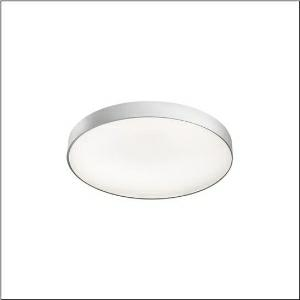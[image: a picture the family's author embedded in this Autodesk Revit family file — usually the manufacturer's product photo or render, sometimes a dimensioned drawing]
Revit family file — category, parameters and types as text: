
# Revit family: round_21_m_51mr36nd0421s
name_source: partatom
category: Lighting Fixtures
units: mm (PartAtom-declared; Revit-internal decimal feet)

## family parameters
Cut with Voids When Loaded = No
Host = Face
Light Source = No
Part Type = Normal
Room Calculation Point = No
Round Connector Dimension = Use Diameter
Shared = No

## types (1)
- Round 21 M (1 x LED, 7470 lm, 54.6 W, 4000K)
    Apparent Load = 55 VA
    CIE Flux Codes = 66 90 98 84 100
    Color Rendering = 80
    Color Temperature = 4000K
    Default Elevation = 1800 mm
    Description = Round 21 M, wall and ceiling luminaire, primary optical cover: micro prismatic cover, of PMMA, transparent, CAT 2 (L<= 3000cd/m²), light emission: direct/indirect distribution, primary light characteristic: symmetric, installation type: surface-mounted, suspended mounting, LED, rated luminous flux: 7.470lm, luminous efficacy: 137lm/W, light colour: 840, colour temperature: 4000K, control gear: DALI 2, with terminal, 5-pole, mains connection: 230V, AC, 50/60Hz, rated input power: 54.6W, housing, of aluminium, coated, silver, diameter: 600mm, height: 62mm, protection rating (complete): IP40, insulation class (complete): insulation class I (protective earthing), certification: CE, impact resistance: IK04, permissible operating ambient temperature: -10..+35°C, packaging unit: 1 piece
    Height = 87 mm
    Lamp = 1 x LED
    Lamp Light Flux = 7470 lm
    Lamp Power = 54.6 W
    Lamp count = 1
    Length = 600 mm
    Luminous efficacy = 137 lm/W
    Manufacturer = Siteco
    ModVariant = No
    Model = 51MR36ND0421S
    Mounting Place = Ceiling
    Mounting Type = Surface mounted
    Number of Poles = 1
    OnlyDefault = Yes
    Power Factor = 1
    Product Name = Round 21 M
    Product group = wall and ceiling luminaire
    ProductGroupID = 304
    Protection Class = Protection class I
    Protection Degree = IP 40
    RLX_Detail_Level = 1
    RLX_Emergency_Light_Flux = 0 lm
    RLX_Emergency_Type = 0
    RLX_Emergency_Type_DB = No
    RlxData = <blob elided: 18989 chars, md5=3c99bea5>
    Socket = socket
    Standby Power = 0 W
    System Light Flux = 7470 lm
    System Power = 55 W
    Type Comments = Product without accessories
    Type Image = l_1258301.jpg
    URL = http://relux.com
    VarID = ---
    Voltage = 0 V
    Weight = 0.00 kg
    Width = 0 mm  [stored 0 ft]

note: [stored X ft] marks values corroborated as IEEE doubles in the binary element streams (Revit-internal decimal feet)

## geometry (parser evidence)
native form markers: Blend x4, Sweep x12
no freeform markers — native parametric forms only
